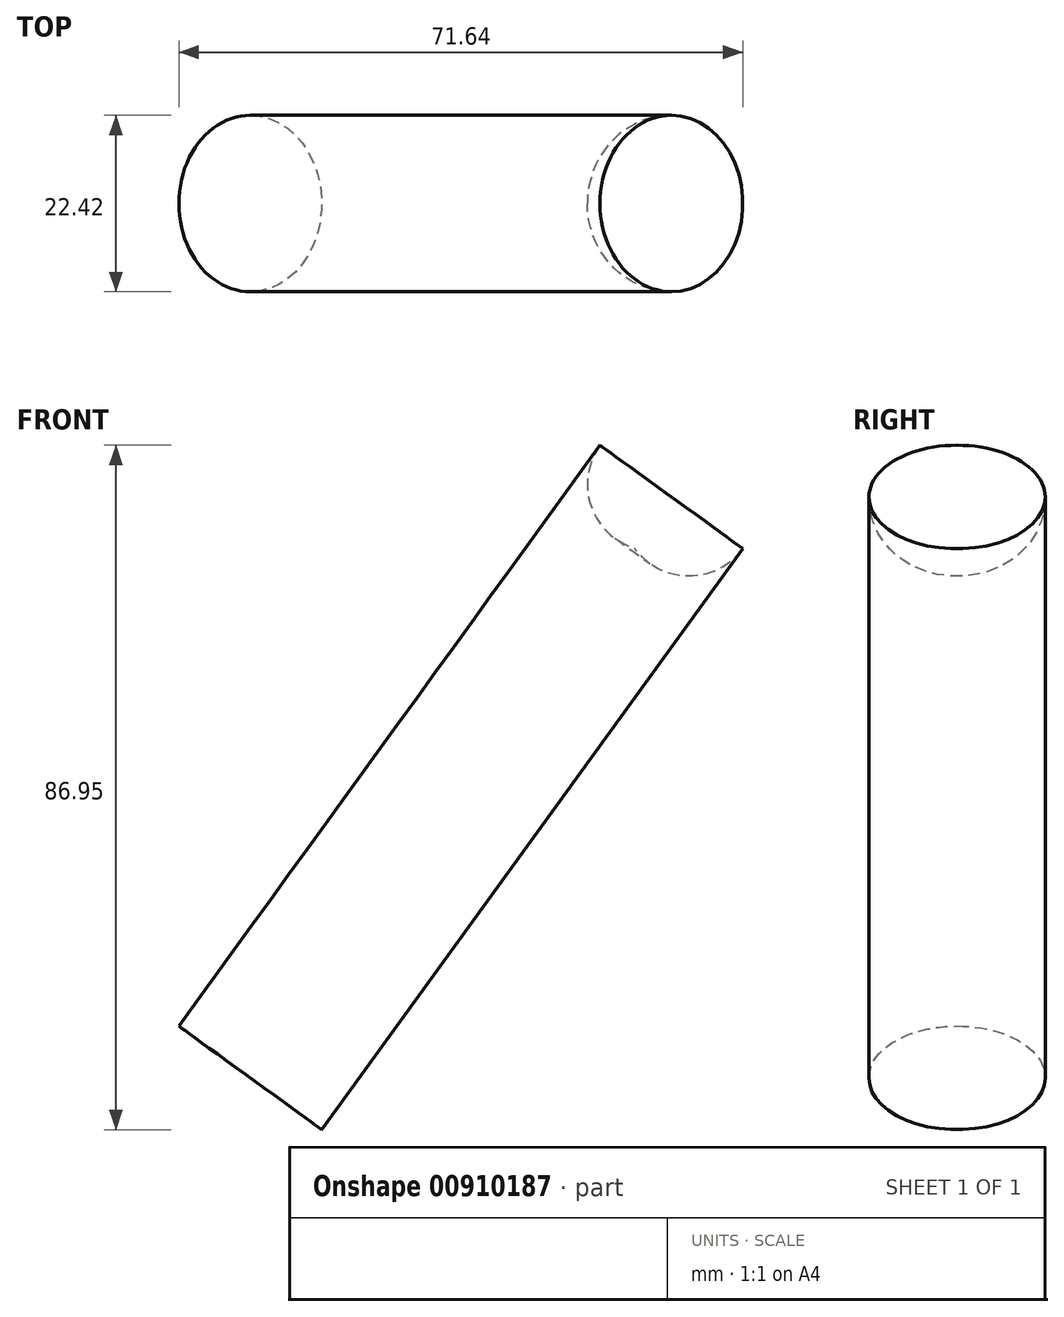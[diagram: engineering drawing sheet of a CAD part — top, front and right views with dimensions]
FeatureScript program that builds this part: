
annotation { "Feature Type Name" : "Feature", "Feature Type Description" : "" }
export const myFeature = defineFeature(function(context is Context, id is Id, definition is map)
    precondition{}
    {
        {
            var Q0;
            Q0=qCreatedBy(makeId("Front.planeOp"),FACE);
            var sketch = newSketch(context, id + "F0", { "sketchPlane" : qUnion([Q0])});
            skLineSegment(sketch, "E0", {"start": v(0, 0) * mm, "end": v(58.2, 80.27) * mm});
            skLineSegment(sketch, "E1", {"start": v(0, 0) * mm, "end": v(9.07, -6.58) * mm});
            skLineSegment(sketch, "E2", {"start": v(9.07, -6.58) * mm, "end": v(62.57, 67.21) * mm});
            skArc(sketch, "E3", {"start": v(62.57, 67.21) * mm, "mid": v(63.74, 74.87) * mm, "end": v(58.2, 80.27) * mm});
            skSolve(sketch);
        }
        {
            var Q0;
            Q0=makeQuery(id+"F0.imprint","IMPRINT",FACE,{"disambiguationData":[TD([[makeQuery(id+"F0.imprint","IMPRINT",EDGE,{"derivedFrom":sQuery(id+"F0.wireOp",EDGE,"E0")}),-1.0]])]});
            var Q1;
            Q1=sQuery(id+"F0.wireOp",EDGE,"E0");
            revolve(context, id + "F1", {"surfaceOperationType" : NewSurfaceOperationType.NEW, "entities" : qUnion([Q0]), "axis" : qUnion([Q1]), "revolveType" : RevolveType.FULL});
        }
    });
